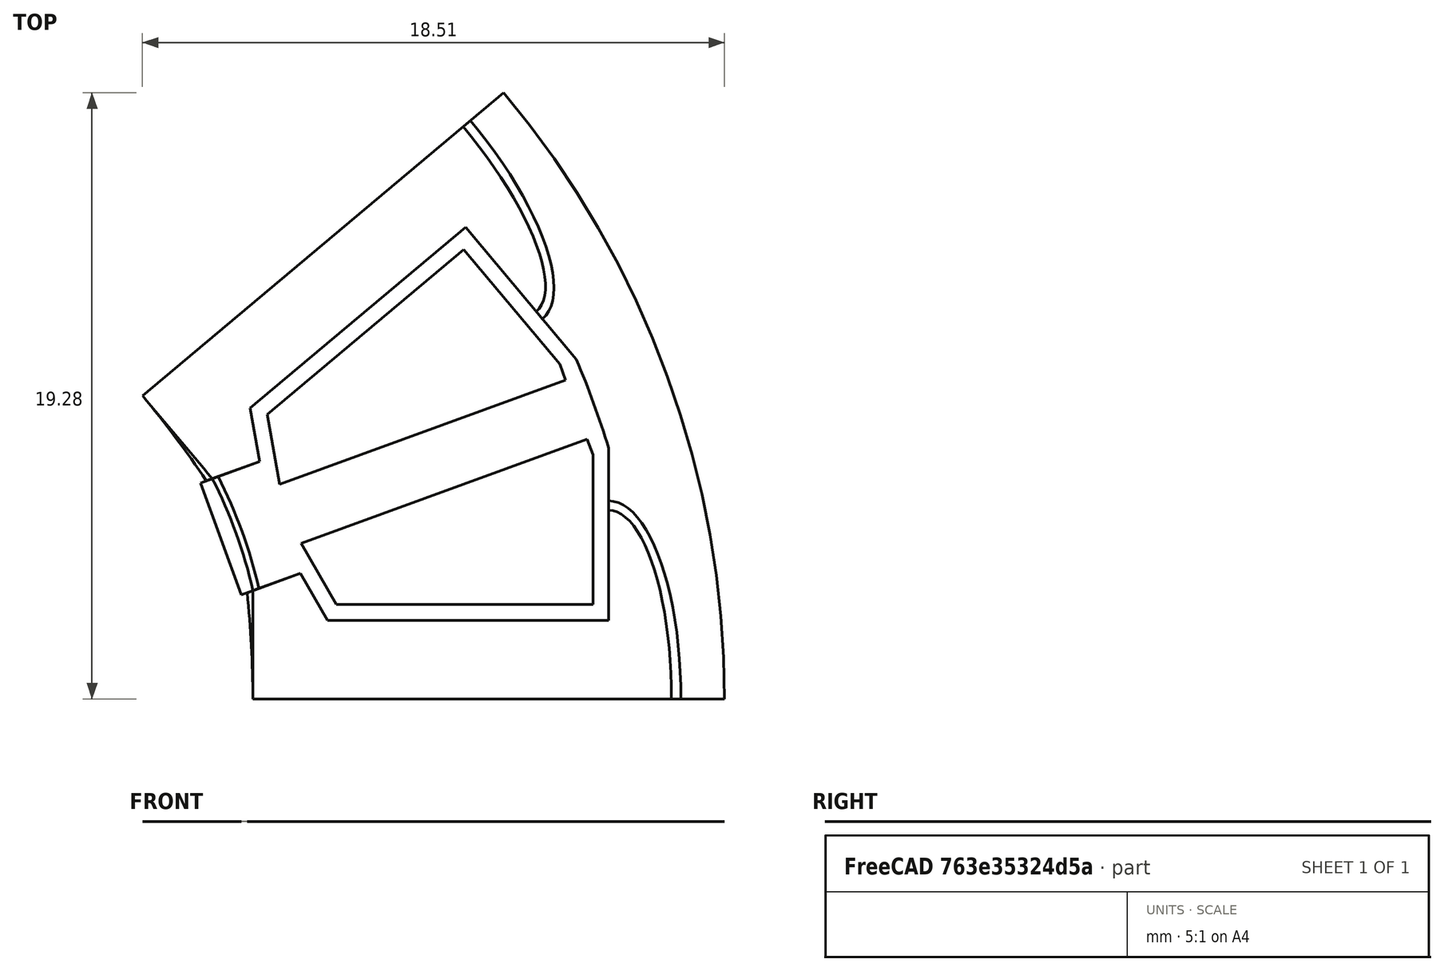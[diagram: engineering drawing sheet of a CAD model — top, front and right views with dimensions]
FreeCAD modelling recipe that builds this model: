
FCSTD DOCUMENT  (FreeCAD 0.18R4 (GitTag))
Label: StatorIRSpokeEllipse
License: All rights reserved
LicenseURL: http://en.wikipedia.org/wiki/All_rights_reserved
objects: Sketcher::SketchObject×10, Surface::Filling×8, PartDesign::Body×2, Spreadsheet::Sheet×1
note: 20 computed .brp shape members not serialized (recipe doc carries the construction recipe); baked Part::Feature solids carry a one-line shape summary decoded from their .brp

FEATURE [Spreadsheet::Sheet] Spreadsheet  label="Variables"
  cells = A2=slotNumber; B2(slotNumber)=9; A3=outerDiameter; B3(outerDiameter)=60; A4=innerDiameter; B4(innerDiameter)=30; A5=stackLength; B5(stackLength)=20; A6=stackingFactor; B6(stackingFactor)=0.95; A7=cuttingThickness; B7(cuttingThickness)=0.1; A8=skewAngle; B8(skewAngle)=0; A9=segmentAngle; B9(segmentAngle)==360 / slotNumber; A10=tipHeightReduction; B10(tipHeightReduction)=20; C10=%; A11=toothThickness; B11(toothThickness)=5; A12=yokeThickness; B12(yokeThickness)=2.5; A13=tipHeight; B13(tipHeight)=2; A14=tipAngle; B14(tipAngle)=120; A15=openingLeft; B15(openingLeft)=1.9; A16=openingRight; B16(openingRight)=1.9; A17=slotIsolation; B17(slotIsolation)=0.5; A18=windingAngle; B18(windingAngle)=35; A19=heightRatio; B19(heightRatio)=45; A20=roundingRadii; B20(roundingRadii)=0.2; A21=backWidth; B21(backWidth)=3; A22=backAngle; B22(backAngle)=90; A23=phaseSeparation; B23(phaseSeparation)=2; A24=axialOverhang; B24(axialOverhang)=1.2; A25=axialHeight; B25(axialHeight)=3; A26=spokeBridgeHeight; B26(spokeBridgeHeight)=0.2; A27=connectionHeight; B27(connectionHeight)=2; A28=connectionWidth; B28(connectionWidth)=12; A29=connectionThickness; B29(connectionThickness)=0.3
FEATURE [Sketcher::SketchObject] Sketch003  label="StatorSketch1"
  MapMode = 5
  Support = -> [XY_Plane]
  expr: Constraints[76] = Variables.backWidth
  expr: Constraints[37] = Variables.tipAngle
  expr: Constraints[60] = Variables.backAngle
  expr: Constraints[30] = Variables.tipHeight
  expr: Constraints[28] = Variables.openingRight
  expr: Constraints[32] = Variables.tipHeight * (1 - Variables.tipHeightReduction / 100)
  expr: Constraints[22] = Variables.openingLeft
  expr: Constraints[6] = Variables.outerDiameter / 2
  expr: Constraints[59] = Variables.tipHeight
  expr: Constraints[5] = Variables.segmentAngle
  expr: Constraints[11] = Variables.innerDiameter / 2
  expr: Constraints[54] = Variables.outerDiameter / 2 - Variables.yokeThickness
  expr: Constraints[49] = Variables.tipHeight * (1 - Variables.tipHeightReduction / 100)
  expr: Constraints[58] = Variables.toothThickness / 2
  expr: Constraints[18] = Variables.segmentAngle / 2
  expr: Constraints[50] = Variables.tipAngle
  expr: Constraints[52] = Variables.backAngle
  expr: Constraints[42] = Variables.toothThickness / 2
  sketch-geometry (27):
    g0: LineSegment [constr] StartX=0 StartY=0 StartZ=0 EndX=22.9813 EndY=19.2836 EndZ=0
    g1: LineSegment [constr] StartX=0 StartY=0 StartZ=0 EndX=30 EndY=0 EndZ=0
    g2: ArcOfCircle CenterX=0 CenterY=0 CenterZ=0 NormalX=0 NormalY=0 NormalZ=1 AngleXU=0 Radius=30 StartAngle=0 EndAngle=0.698132
    g3: ArcOfCircle [constr] CenterX=0 CenterY=0 CenterZ=0 NormalX=0 NormalY=0 NormalZ=1 AngleXU=0 Radius=15 StartAngle=0 EndAngle=0.698132
    g4: LineSegment [constr] StartX=13.3338 StartY=6.87098 StartZ=0 EndX=27.4859 EndY=12.0219 EndZ=0
    g5: LineSegment [constr] StartX=14.6308 StartY=3.30731 StartZ=0 EndX=28.7829 EndY=8.45826 EndZ=0
    g6: LineSegment [constr] StartX=28.1908 StartY=10.2606 StartZ=0 EndX=14.0954 EndY=5.1303 EndZ=0
    g7: LineSegment [constr] StartX=0 StartY=0 StartZ=0 EndX=14.0954 EndY=5.1303 EndZ=0
    g8: LineSegment [constr] StartX=13.3338 StartY=6.87098 StartZ=0 EndX=14.0954 EndY=5.1303 EndZ=0
    g9: LineSegment [constr] StartX=14.0954 StartY=5.1303 StartZ=0 EndX=14.6308 EndY=3.30731 EndZ=0
    g10: LineSegment [constr] StartX=13.5217 StartY=6.93938 StartZ=0 EndX=15.2132 EndY=7.55502 EndZ=0
    g11: LineSegment StartX=13.5217 StartY=6.93938 StartZ=0 EndX=15.2132 EndY=7.55502 EndZ=0
    g12: LineSegment StartX=15.2132 StartY=7.55502 StartZ=0 EndX=14.9141 EndY=9.25092 EndZ=0
    g13: LineSegment StartX=14.9141 StartY=9.25092 StartZ=0 EndX=21.7663 EndY=15.0006 EndZ=0
    g14: LineSegment [constr] StartX=14.9141 StartY=9.25092 StartZ=0 EndX=13.3072 EndY=11.166 EndZ=0
    g15: LineSegment StartX=21.7663 StartY=15.0006 StartZ=0 EndX=25.29 EndY=10.8011 EndZ=0
    g16: LineSegment StartX=26.3161 StartY=7.98201 StartZ=0 EndX=26.3161 EndY=2.5 EndZ=0
    g17: LineSegment StartX=26.3161 StartY=2.5 StartZ=0 EndX=17.3713 EndY=2.5 EndZ=0
    g18: LineSegment StartX=17.3713 StartY=2.5 StartZ=0 EndX=16.5102 EndY=3.99135 EndZ=0
    g19: LineSegment StartX=16.5102 StartY=3.99135 StartZ=0 EndX=14.8188 EndY=3.37572 EndZ=0
    g20: LineSegment [constr] StartX=26.3161 StartY=2.5 StartZ=0 EndX=26.3161 EndY=0 EndZ=0
    g21: LineSegment StartX=11.4907 StartY=9.64181 StartZ=0 EndX=22.9813 EndY=19.2836 EndZ=0
    g22: LineSegment StartX=30 StartY=0 StartZ=0 EndX=15 EndY=0 EndZ=0
    g23: ArcOfCircle CenterX=-16.5325 CenterY=0 CenterZ=0 NormalX=0 NormalY=0 NormalZ=1 AngleXU=0 Radius=31.5325 StartAngle=0 EndAngle=0.107261
    g24: ArcOfCircle CenterX=-12.6646 CenterY=-10.6269 CenterZ=0 NormalX=0 NormalY=0 NormalZ=1 AngleXU=0 Radius=31.5325 StartAngle=0.590871 EndAngle=0.698132
    g25: ArcOfCircle CenterX=0 CenterY=0 CenterZ=0 NormalX=0 NormalY=0 NormalZ=1 AngleXU=0 Radius=27.5 StartAngle=0.294493 EndAngle=0.403638
    g26: LineSegment [constr] StartX=25.29 StartY=10.8011 StartZ=0 EndX=26.3161 EndY=7.98201 EndZ=0
  constraints (77):
    c: Angle(g-1,g1) = 0
    c: Coincident(g0,g-1)
    c: Coincident(g1,g-1)
    c: Coincident(g2,g-1)
    c: Coincident(g2,g0)
    c: Angle(g1,g0) = 0.698132
    c: Radius(g2) = 30
    c: Coincident(g2,g1)
    c: Coincident(g3,g-1)
    c: PointOnObject(g3,g1)
    c: PointOnObject(g3,g0)
    c: Radius(g3) = 15
    c: PointOnObject(g4,g3)
    c: PointOnObject(g4,g2)
    c: PointOnObject(g5,g3)
    c: PointOnObject(g5,g2)
    c: PointOnObject(g6,g2)
    c: PointOnObject(g6,g3)
    c: Angle(g1,g6) = 0.349066
    c: Coincident(g7,g-1)
    c: Coincident(g7,g6)
    c: Coincident(g8,g4)
    c: Distance(g8) = 1.9
    c: Coincident(g8,g6)
    c: Parallel(g4,g6)
    c: Parallel(g5,g6)
    c: Coincident(g9,g6)
    c: Coincident(g9,g5)
    c: Distance(g9) = 1.9
    c: PointOnObject(g10,g4)
    c: Distance(g4,g10) = 2
    c: Angle(g4,g10) = 3.14159
    c: Distance(g10,g10) = 1.6
    c: Coincident(g11,g10)
    c: Coincident(g12,g11)
    c: Coincident(g13,g12)
    c: Coincident(g11,g10)
    c: Angle(g12,g13) = 2.0944
    c: Parallel(g0,g13)
    c: Coincident(g14,g12)
    c: PointOnObject(g14,g0)
    c: Angle(g13,g14) = 1.5708
    c: Distance(g14) = 2.5
    c: Coincident(g15,g13)
    c: Coincident(g17,g16)
    c: Coincident(g18,g17)
    c: PointOnObject(g18,g5)
    c: Coincident(g19,g18)
    c: PointOnObject(g19,g5)
    c: Distance(g19) = 1.6
    c: Angle(g17,g18) = 2.0944
    c: Parallel(g17,g1)
    c: Angle(g16,g17) = 1.5708
    c: Symmetric(g15,g16,g6)
    c: Distance(g-1,g15) = 27.5
    c: Coincident(g20,g16)
    c: PointOnObject(g20,g1)
    c: Vertical(g20)
    c: DistanceY(g20,g20) = 2.5
    c: Distance(g5,g18) = 2
    c: Angle(g13,g15) = 1.5708
    c: Coincident(g21,g3)
    c: Coincident(g21,g0)
    c: Coincident(g22,g2)
    c: Coincident(g22,g3)
    c: PointOnObject(g23,g-1)
    c: Coincident(g23,g19)
    c: Coincident(g23,g22)
    c: PointOnObject(g24,g0)
    c: Coincident(g24,g11)
    c: Coincident(g24,g21)
    c: Coincident(g25,g2)
    c: Coincident(g25,g15)
    c: Coincident(g25,g16)
    c: Coincident(g26,g15)
    c: Coincident(g26,g16)
    c: Distance(g26) = 3
FEATURE [Sketcher::SketchObject] Sketch  label="StatorStack"
  MapMode = 5
  Support = -> [XY_Plane001]
  expr: Constraints[20] = Variables.innerDiameter / 2
  expr: Constraints[10] = Variables.outerDiameter / 2
  expr: Constraints[9] = Variables.innerDiameter / 2
  expr: Constraints[8] = Variables.stackLength
  sketch-geometry (8):
    g0: LineSegment StartX=-10 StartY=15 StartZ=0 EndX=10 EndY=15 EndZ=0
    g1: LineSegment StartX=10 StartY=15 StartZ=0 EndX=10 EndY=30 EndZ=0
    g2: LineSegment StartX=10 StartY=30 StartZ=0 EndX=-10 EndY=30 EndZ=0
    g3: LineSegment StartX=-10 StartY=30 StartZ=0 EndX=-10 EndY=15 EndZ=0
    g4: LineSegment StartX=-10 StartY=-15 StartZ=0 EndX=10 EndY=-15 EndZ=0
    g5: LineSegment StartX=10 StartY=-15 StartZ=0 EndX=10 EndY=-30 EndZ=0
    g6: LineSegment StartX=10 StartY=-30 StartZ=0 EndX=-10 EndY=-30 EndZ=0
    g7: LineSegment StartX=-10 StartY=-30 StartZ=0 EndX=-10 EndY=-15 EndZ=0
  constraints (22):
    c: Coincident(g0,g1)
    c: Coincident(g1,g2)
    c: Coincident(g2,g3)
    c: Coincident(g3,g0)
    c: Horizontal(g2)
    c: Vertical(g1)
    c: Vertical(g3)
    c: Symmetric(g0,g0,g-2)
    c: DistanceX(g0,g0) = 20
    c: DistanceY(g-1,g0) = 15
    c: DistanceY(g-1,g1) = 30
    c: Coincident(g4,g5)
    c: Coincident(g5,g6)
    c: Coincident(g6,g7)
    c: Coincident(g7,g4)
    c: Horizontal(g6)
    c: Vertical(g5)
    c: Vertical(g7)
    c: Equal(g4,g0)
    c: Symmetric(g4,g4,g-2)
    c: DistanceY(g4,g-1) = 15
    c: Equal(g7,g3)
FEATURE [Sketcher::SketchObject] Sketch005  label="StatorSketch2"
  MapMode = 5
  Support = -> [XY_Plane]
  expr: Constraints[76] = Variables.backWidth
  expr: Constraints[30] = Variables.tipHeight
  expr: Constraints[51] = Variables.tipAngle
  expr: Constraints[28] = Variables.openingRight
  expr: Constraints[37] = Variables.tipAngle
  expr: Constraints[60] = Variables.tipHeight
  expr: Constraints[32] = Variables.tipHeight * (1 - Variables.tipHeightReduction / 100)
  expr: Constraints[61] = Variables.backAngle
  expr: Constraints[6] = Variables.outerDiameter / 2
  expr: Constraints[5] = Variables.segmentAngle
  expr: Constraints[22] = Variables.openingLeft
  expr: Constraints[55] = Variables.outerDiameter / 2 - Variables.yokeThickness
  expr: Constraints[59] = Variables.toothThickness / 2
  expr: Constraints[50] = Variables.tipHeight * (1 - Variables.tipHeightReduction / 100)
  expr: Constraints[18] = Variables.segmentAngle / 2
  expr: Constraints[11] = Variables.innerDiameter / 2
  expr: Constraints[53] = Variables.backAngle
  expr: Constraints[42] = Variables.toothThickness / 2
  sketch-geometry (27):
    g0: LineSegment [constr] StartX=0 StartY=0 StartZ=0 EndX=22.9813 EndY=19.2836 EndZ=0
    g1: LineSegment [constr] StartX=0 StartY=0 StartZ=0 EndX=30 EndY=0 EndZ=0
    g2: ArcOfCircle CenterX=0 CenterY=0 CenterZ=0 NormalX=0 NormalY=0 NormalZ=1 AngleXU=0 Radius=30 StartAngle=0 EndAngle=0.698132
    g3: ArcOfCircle [constr] CenterX=0 CenterY=0 CenterZ=0 NormalX=0 NormalY=0 NormalZ=1 AngleXU=0 Radius=15 StartAngle=0 EndAngle=0.698132
    g4: LineSegment [constr] StartX=13.3338 StartY=6.87098 StartZ=0 EndX=27.4859 EndY=12.0219 EndZ=0
    g5: LineSegment [constr] StartX=14.6308 StartY=3.30731 StartZ=0 EndX=28.7829 EndY=8.45826 EndZ=0
    g6: LineSegment [constr] StartX=28.1908 StartY=10.2606 StartZ=0 EndX=14.0954 EndY=5.1303 EndZ=0
    g7: LineSegment [constr] StartX=0 StartY=0 StartZ=0 EndX=14.0954 EndY=5.1303 EndZ=0
    g8: LineSegment [constr] StartX=13.3338 StartY=6.87098 StartZ=0 EndX=14.0954 EndY=5.1303 EndZ=0
    g9: LineSegment [constr] StartX=14.0954 StartY=5.1303 StartZ=0 EndX=14.6308 EndY=3.30731 EndZ=0
    g10: LineSegment [constr] StartX=13.7097 StartY=7.00779 StartZ=0 EndX=15.2132 EndY=7.55502 EndZ=0
    g11: LineSegment StartX=13.7097 StartY=7.00779 StartZ=0 EndX=15.2132 EndY=7.55502 EndZ=0
    g12: LineSegment StartX=15.2132 StartY=7.55502 StartZ=0 EndX=14.9141 EndY=9.25092 EndZ=0
    g13: LineSegment StartX=14.9141 StartY=9.25092 StartZ=0 EndX=21.7663 EndY=15.0006 EndZ=0
    g14: LineSegment [constr] StartX=14.9141 StartY=9.25092 StartZ=0 EndX=13.3072 EndY=11.166 EndZ=0
    g15: LineSegment StartX=21.7663 StartY=15.0006 StartZ=0 EndX=25.29 EndY=10.8011 EndZ=0
    g16: LineSegment [constr] StartX=25.29 StartY=10.8011 StartZ=0 EndX=26.3161 EndY=7.98201 EndZ=0
    g17: LineSegment StartX=26.3161 StartY=7.98201 StartZ=0 EndX=26.3161 EndY=2.5 EndZ=0
    g18: LineSegment StartX=26.3161 StartY=2.5 StartZ=0 EndX=17.3713 EndY=2.5 EndZ=0
    g19: LineSegment StartX=17.3713 StartY=2.5 StartZ=0 EndX=16.5102 EndY=3.99135 EndZ=0
    g20: LineSegment StartX=16.5102 StartY=3.99135 StartZ=0 EndX=15.0067 EndY=3.44412 EndZ=0
    g21: LineSegment [constr] StartX=26.3161 StartY=2.5 StartZ=0 EndX=26.3161 EndY=0 EndZ=0
    g22: LineSegment StartX=11.4907 StartY=9.64181 StartZ=0 EndX=22.9813 EndY=19.2836 EndZ=0
    g23: LineSegment StartX=30 StartY=0 StartZ=0 EndX=15 EndY=1.08e-13 EndZ=0
    g24: ArcOfCircle CenterX=687.223 CenterY=576.649 CenterZ=0 NormalX=0 NormalY=0 NormalZ=1 AngleXU=0 Radius=882.106 StartAngle=3.83972 EndAngle=3.84363
    g25: ArcOfCircle CenterX=897.106 CenterY=0 CenterZ=0 NormalX=0 NormalY=0 NormalZ=1 AngleXU=0 Radius=882.106 StartAngle=3.13769 EndAngle=3.14159
    g26: ArcOfCircle CenterX=0 CenterY=0 CenterZ=0 NormalX=0 NormalY=0 NormalZ=1 AngleXU=0 Radius=27.5 StartAngle=0.294493 EndAngle=0.403638
  constraints (77):
    c: Angle(g-1,g1) = 0
    c: Coincident(g0,g-1)
    c: Coincident(g1,g-1)
    c: Coincident(g2,g-1)
    c: Coincident(g2,g0)
    c: Angle(g1,g0) = 0.698132
    c: Radius(g2) = 30
    c: Coincident(g2,g1)
    c: Coincident(g3,g-1)
    c: PointOnObject(g3,g1)
    c: PointOnObject(g3,g0)
    c: Radius(g3) = 15
    c: PointOnObject(g4,g3)
    c: PointOnObject(g4,g2)
    c: PointOnObject(g5,g3)
    c: PointOnObject(g5,g2)
    c: PointOnObject(g6,g2)
    c: PointOnObject(g6,g3)
    c: Angle(g1,g6) = 0.349066
    c: Coincident(g7,g-1)
    c: Coincident(g7,g6)
    c: Coincident(g8,g4)
    c: Distance(g8) = 1.9
    c: Coincident(g8,g6)
    c: Parallel(g4,g6)
    c: Parallel(g5,g6)
    c: Coincident(g9,g6)
    c: Coincident(g9,g5)
    c: Distance(g9) = 1.9
    c: PointOnObject(g10,g4)
    c: Distance(g4,g10) = 2
    c: Angle(g4,g10) = 3.14159
    c: Distance(g10,g10) = 1.6
    c: Coincident(g11,g10)
    c: Coincident(g12,g11)
    c: Coincident(g13,g12)
    c: Coincident(g11,g10)
    c: Angle(g12,g13) = 2.0944
    c: Parallel(g0,g13)
    c: Coincident(g14,g12)
    c: PointOnObject(g14,g0)
    c: Angle(g13,g14) = 1.5708
    c: Distance(g14) = 2.5
    c: Coincident(g15,g13)
    c: Coincident(g16,g15)
    c: Coincident(g17,g16)
    c: Coincident(g18,g17)
    c: Coincident(g19,g18)
    c: PointOnObject(g19,g5)
    c: Coincident(g20,g19)
    c: Distance(g20) = 1.6
    c: Angle(g18,g19) = 2.0944
    c: Parallel(g18,g1)
    c: Angle(g17,g18) = 1.5708
    c: Symmetric(g15,g16,g6)
    c: Distance(g-1,g15) = 27.5
    c: Coincident(g21,g17)
    c: PointOnObject(g21,g1)
    c: Vertical(g21)
    c: DistanceY(g21,g21) = 2.5
    c: Distance(g5,g19) = 2
    c: Angle(g13,g15) = 1.5708
    c: Coincident(g22,g3)
    c: Coincident(g22,g0)
    c: Coincident(g23,g2)
    c: Coincident(g23,g3)
    c: PointOnObject(g24,g22)
    c: Coincident(g24,g11)
    c: Coincident(g24,g22)
    c: Angle(g5,g20) = 3.14159
    c: PointOnObject(g25,g-1)
    c: Coincident(g25,g20)
    c: Coincident(g25,g23)
    c: Coincident(g26,g2)
    c: Coincident(g26,g15)
    c: Coincident(g26,g17)
    c: Distance(g16) = 3
FEATURE [Sketcher::SketchObject] Sketch008  label="SlotSketch"
  MapMode = 5
  Support = -> [XY_Plane]
  expr: Constraints[50] = Variables.toothThickness / 2
  expr: Constraints[18] = Variables.segmentAngle / 2
  expr: Constraints[30] = Variables.tipAngle
  expr: Constraints[51] = Variables.tipHeight
  expr: Constraints[28] = Variables.openingRight
  expr: Constraints[67] = Variables.backWidth
  expr: Constraints[46] = Variables.outerDiameter / 2 - Variables.yokeThickness
  expr: Constraints[22] = Variables.openingLeft
  expr: Constraints[6] = Variables.outerDiameter / 2
  expr: Constraints[44] = Variables.backAngle
  expr: Constraints[52] = Variables.backAngle
  expr: Constraints[11] = Variables.innerDiameter / 2
  expr: Constraints[5] = Variables.segmentAngle
  expr: Constraints[42] = Variables.tipAngle
  expr: Constraints[35] = Variables.toothThickness / 2
  sketch-geometry (25):
    g0: LineSegment [constr] StartX=0 StartY=0 StartZ=0 EndX=22.9813 EndY=19.2836 EndZ=0
    g1: LineSegment [constr] StartX=0 StartY=0 StartZ=0 EndX=30 EndY=0 EndZ=0
    g2: ArcOfCircle [constr] CenterX=0 CenterY=0 CenterZ=0 NormalX=0 NormalY=0 NormalZ=1 AngleXU=0 Radius=30 StartAngle=0 EndAngle=0.698132
    g3: ArcOfCircle [constr] CenterX=0 CenterY=0 CenterZ=0 NormalX=0 NormalY=0 NormalZ=1 AngleXU=0 Radius=15 StartAngle=0 EndAngle=0.698132
    g4: LineSegment [constr] StartX=13.3338 StartY=6.87098 StartZ=0 EndX=27.4859 EndY=12.0219 EndZ=0
    g5: LineSegment [constr] StartX=14.6308 StartY=3.30731 StartZ=0 EndX=28.7829 EndY=8.45826 EndZ=0
    g6: LineSegment [constr] StartX=28.1908 StartY=10.2606 StartZ=0 EndX=14.0954 EndY=5.1303 EndZ=0
    g7: LineSegment [constr] StartX=0 StartY=0 StartZ=0 EndX=14.0954 EndY=5.1303 EndZ=0
    g8: LineSegment [constr] StartX=13.3338 StartY=6.87098 StartZ=0 EndX=14.0954 EndY=5.1303 EndZ=0
    g9: LineSegment [constr] StartX=14.0954 StartY=5.1303 StartZ=0 EndX=14.6308 EndY=3.30731 EndZ=0
    g10: LineSegment StartX=15.2132 StartY=7.55502 StartZ=0 EndX=14.9141 EndY=9.25092 EndZ=0
    g11: LineSegment StartX=14.9141 StartY=9.25092 StartZ=0 EndX=21.7663 EndY=15.0006 EndZ=0
    g12: LineSegment [constr] StartX=14.9141 StartY=9.25092 StartZ=0 EndX=13.3072 EndY=11.166 EndZ=0
    g13: LineSegment StartX=21.7663 StartY=15.0006 StartZ=0 EndX=25.29 EndY=10.8011 EndZ=0
    g14: LineSegment [constr] StartX=25.29 StartY=10.8011 StartZ=0 EndX=26.3161 EndY=7.98201 EndZ=0
    g15: LineSegment StartX=26.3161 StartY=7.98201 StartZ=0 EndX=26.3161 EndY=2.5 EndZ=0
    g16: LineSegment StartX=26.3161 StartY=2.5 StartZ=0 EndX=17.3713 EndY=2.5 EndZ=0
    g17: LineSegment StartX=17.3713 StartY=2.5 StartZ=0 EndX=16.5102 EndY=3.99135 EndZ=0
    g18: LineSegment [constr] StartX=26.3161 StartY=2.5 StartZ=0 EndX=26.3161 EndY=0 EndZ=0
    g19: LineSegment [constr] StartX=11.4907 StartY=9.64181 StartZ=0 EndX=22.9813 EndY=19.2836 EndZ=0
    g20: LineSegment [constr] StartX=30 StartY=0 StartZ=0 EndX=15 EndY=0 EndZ=0
    g21: LineSegment StartX=13.3338 StartY=6.87098 StartZ=0 EndX=14.6308 EndY=3.30731 EndZ=0
    g22: LineSegment StartX=13.3338 StartY=6.87098 StartZ=0 EndX=15.2132 EndY=7.55502 EndZ=0
    g23: LineSegment StartX=14.6308 StartY=3.30731 StartZ=0 EndX=16.5102 EndY=3.99135 EndZ=0
    g24: ArcOfCircle CenterX=0 CenterY=0 CenterZ=0 NormalX=0 NormalY=0 NormalZ=1 AngleXU=0 Radius=27.5 StartAngle=0.294493 EndAngle=0.403638
  constraints (68):
    c: Angle(g-1,g1) = 0
    c: Coincident(g0,g-1)
    c: Coincident(g1,g-1)
    c: Coincident(g2,g-1)
    c: Coincident(g2,g0)
    c: Angle(g1,g0) = 0.698132
    c: Radius(g2) = 30
    c: Coincident(g2,g1)
    c: Coincident(g3,g-1)
    c: PointOnObject(g3,g1)
    c: PointOnObject(g3,g0)
    c: Radius(g3) = 15
    c: PointOnObject(g4,g3)
    c: PointOnObject(g4,g2)
    c: PointOnObject(g5,g3)
    c: PointOnObject(g5,g2)
    c: PointOnObject(g6,g2)
    c: PointOnObject(g6,g3)
    c: Angle(g1,g6) = 0.349066
    c: Coincident(g7,g-1)
    c: Coincident(g7,g6)
    c: Coincident(g8,g4)
    c: Distance(g8) = 1.9
    c: Coincident(g8,g6)
    c: Parallel(g4,g6)
    c: Parallel(g5,g6)
    c: Coincident(g9,g6)
    c: Coincident(g9,g5)
    c: Distance(g9) = 1.9
    c: Coincident(g11,g10)
    c: Angle(g10,g11) = 2.0944
    c: Parallel(g0,g11)
    c: Coincident(g12,g10)
    c: PointOnObject(g12,g0)
    c: Angle(g11,g12) = 1.5708
    c: Distance(g12) = 2.5
    c: Coincident(g13,g11)
    c: Coincident(g14,g13)
    c: Coincident(g15,g14)
    c: Coincident(g16,g15)
    c: Coincident(g17,g16)
    c: PointOnObject(g17,g5)
    c: Angle(g16,g17) = 2.0944
    c: Parallel(g16,g1)
    c: Angle(g15,g16) = 1.5708
    c: Symmetric(g13,g14,g6)
    c: Distance(g-1,g13) = 27.5
    c: Coincident(g18,g15)
    c: PointOnObject(g18,g1)
    c: Vertical(g18)
    c: DistanceY(g18,g18) = 2.5
    c: Distance(g5,g17) = 2
    c: Angle(g11,g13) = 1.5708
    c: Coincident(g19,g3)
    c: Coincident(g19,g0)
    c: Coincident(g20,g2)
    c: Coincident(g20,g3)
    c: Symmetric(g17,g10,g6)
    c: Coincident(g21,g4)
    c: Coincident(g21,g5)
    c: Coincident(g22,g21)
    c: Coincident(g22,g10)
    c: Coincident(g23,g21)
    c: Coincident(g23,g17)
    c: Coincident(g24,g-1)
    c: Coincident(g24,g13)
    c: Coincident(g24,g15)
    c: Distance(g14) = 3
FEATURE [Sketcher::SketchObject] Sketch006  label="TerminalLeftSketch"
  ExternalGeometry = -> [Sketch008]
  MapMode = 5
  Support = -> [XY_Plane]
  expr: Constraints[28] = abs(Variables.backWidth - Variables.phaseSeparation) / 2 + Variables.slotIsolation / 15
  expr: Constraints[21] = Variables.slotIsolation
  expr: Constraints[14] = Variables.phaseSeparation / 2
  sketch-geometry (10):
    g0: LineSegment StartX=24.7672 StartY=10.6463 StartZ=0 EndX=21.7046 EndY=14.2961 EndZ=0
    g1: LineSegment StartX=21.7046 StartY=14.2961 StartZ=0 EndX=15.4567 EndY=9.05346 EndZ=0
    g2: LineSegment StartX=15.4567 StartY=9.05346 StartZ=0 EndX=15.8483 EndY=6.83248 EndZ=0
    g3: LineSegment StartX=15.8483 StartY=6.83248 StartZ=0 EndX=24.9497 EndY=10.1451 EndZ=0
    g4: LineSegment StartX=24.9497 StartY=10.1451 StartZ=0 EndX=24.7672 EndY=10.6463 EndZ=0
    g5: LineSegment [constr] StartX=0 StartY=0 StartZ=0 EndX=15.8617 EndY=5.77319 EndZ=0
    g6: LineSegment [constr] StartX=15.8483 StartY=6.83248 StartZ=0 EndX=16.1903 EndY=5.89279 EndZ=0
    g7: LineSegment [constr] StartX=21.7046 StartY=14.2961 StartZ=0 EndX=22.0877 EndY=14.6175 EndZ=0
    g8: LineSegment [constr] StartX=21.7046 StartY=14.2961 StartZ=0 EndX=21.3833 EndY=14.6792 EndZ=0
    g9: LineSegment [constr] StartX=15.4567 StartY=9.05346 StartZ=0 EndX=14.9643 EndY=8.96663 EndZ=0
  constraints (29):
    c: Coincident(g1,g0)
    c: Coincident(g2,g1)
    c: Coincident(g3,g2)
    c: Coincident(g4,g3)
    c: Coincident(g4,g0)
    c: Parallel(g1,g-4)
    c: Parallel(g-5,g2)
    c: Parallel(g0,g-3)
    c: Angle(g4,g3) = 1.5708
    c: Symmetric(g-5,g-6,g5)
    c: Parallel(g3,g5)
    c: Coincident(g6,g2)
    c: PointOnObject(g6,g5)
    c: Angle(g6,g5) = 1.5708
    c: Distance(g6) = 1
    c: Coincident(g7,g0)
    c: PointOnObject(g7,g-3)
    c: Coincident(g8,g0)
    c: PointOnObject(g8,g-4)
    c: Angle(g0,g7) = 1.5708
    c: Angle(g8,g1) = 1.5708
    c: Distance(g8) = 0.5
    c: Equal(g8,g7)
    c: Coincident(g5,g-1)
    c: Coincident(g9,g1)
    c: PointOnObject(g9,g-5)
    c: Angle(g-5,g9) = 1.5708
    c: Equal(g8,g9)
    c: Distance(g4) = 0.533333
FEATURE [Sketcher::SketchObject] Sketch007  label="TerminalRightSketch"
  ExternalGeometry = -> [Sketch008]
  MapMode = 5
  Support = -> [XY_Plane]
  expr: Constraints[27] = Variables.slotIsolation
  expr: Constraints[26] = abs(Variables.backWidth - Variables.phaseSeparation) / 2 + Variables.slotIsolation / 15
  expr: Constraints[13] = Variables.phaseSeparation / 2
  sketch-geometry (10):
    g0: LineSegment [constr] StartX=0 StartY=0 StartZ=0 EndX=15.8617 EndY=5.77319 EndZ=0
    g1: LineSegment StartX=25.8161 StartY=7.76456 StartZ=0 EndX=25.8161 EndY=3 EndZ=0
    g2: LineSegment StartX=25.8161 StartY=3 StartZ=0 EndX=17.6599 EndY=3 EndZ=0
    g3: LineSegment StartX=17.6599 StartY=3 StartZ=0 EndX=16.5323 EndY=4.95309 EndZ=0
    g4: LineSegment StartX=16.5323 StartY=4.95309 StartZ=0 EndX=25.6337 EndY=8.26572 EndZ=0
    g5: LineSegment StartX=25.6337 StartY=8.26572 StartZ=0 EndX=25.8161 EndY=7.76456 EndZ=0
    g6: LineSegment [constr] StartX=16.5323 StartY=4.95309 StartZ=0 EndX=16.1903 EndY=5.89279 EndZ=0
    g7: LineSegment [constr] StartX=25.8161 StartY=3 StartZ=0 EndX=25.8161 EndY=2.5 EndZ=0
    g8: LineSegment [constr] StartX=25.8161 StartY=3 StartZ=0 EndX=26.3161 EndY=3 EndZ=0
    g9: LineSegment [constr] StartX=17.6599 StartY=3 StartZ=0 EndX=17.2269 EndY=2.75 EndZ=0
  constraints (29):
    c: Symmetric(g-5,g-6,g0)
    c: Coincident(g0,g-1)
    c: Vertical(g1)
    c: Coincident(g2,g1)
    c: Horizontal(g2)
    c: Coincident(g3,g2)
    c: Coincident(g4,g3)
    c: Coincident(g5,g4)
    c: Coincident(g5,g1)
    c: Parallel(g0,g4)
    c: Coincident(g6,g3)
    c: PointOnObject(g6,g0)
    c: Angle(g0,g6) = 1.5708
    c: Distance(g6) = 1
    c: Angle(g4,g5) = 1.5708
    c: Coincident(g7,g1)
    c: PointOnObject(g7,g-7)
    c: Coincident(g8,g1)
    c: PointOnObject(g8,g-8)
    c: Angle(g8,g1) = 1.5708
    c: Angle(g2,g7) = 1.5708
    c: Equal(g8,g7)
    c: Parallel(g3,g-6)
    c: Coincident(g9,g2)
    c: PointOnObject(g9,g-6)
    c: Angle(g3,g9) = 1.5708
    c: Distance(g5) = 0.533333
    c: Distance(g8) = 0.5
    c: Equal(g8,g9)
FEATURE [Surface::Filling] Surface  label="SlotSketch_Surface"
  Anisotropy = false
  BoundaryEdges = -> [Sketch008]
  BoundaryOrder = [0,0,0,0,0,0,0,0,0,0]
  Degree = 3
  Iterations = 2
  MaximumDegree = 8
  MaximumSegments = 9
  PointsOnCurve = 15
  TolAngular = 0.01
  TolCurvature = 0.1
  Tolerance2d = 1e-05
  Tolerance3d = 0.0001
FEATURE [Surface::Filling] Surface001  label="StatorSketch2_Surface"
  Anisotropy = false
  BoundaryEdges = -> [Sketch005]
  BoundaryOrder = [0,0,0,0,0,0,0,0,0,0,0,0,0,0]
  Degree = 3
  Iterations = 2
  MaximumDegree = 8
  MaximumSegments = 9
  PointsOnCurve = 15
  TolAngular = 0.01
  TolCurvature = 0.1
  Tolerance2d = 1e-05
  Tolerance3d = 0.0001
FEATURE [Surface::Filling] Surface002  label="StatorSketch1_Surface"
  Anisotropy = false
  BoundaryEdges = -> [Sketch003]
  BoundaryOrder = [0,0,0,0,0,0,0,0,0,0,0,0,0,0]
  Degree = 3
  Iterations = 2
  MaximumDegree = 8
  MaximumSegments = 9
  PointsOnCurve = 15
  TolAngular = 0.01
  TolCurvature = 0.1
  Tolerance2d = 1e-05
  Tolerance3d = 0.0001
FEATURE [Surface::Filling] Surface003  label="TerminalRightSketch_Surface"
  Anisotropy = false
  BoundaryEdges = -> [Sketch007]
  BoundaryOrder = [0,0,0,0,0]
  Degree = 3
  Iterations = 2
  MaximumDegree = 8
  MaximumSegments = 9
  PointsOnCurve = 15
  TolAngular = 0.01
  TolCurvature = 0.1
  Tolerance2d = 1e-05
  Tolerance3d = 0.0001
FEATURE [Surface::Filling] Surface004  label="TerminalLeftSketch_Surface"
  Anisotropy = false
  BoundaryEdges = -> [Sketch006]
  BoundaryOrder = [0,0,0,0,0]
  Degree = 3
  Iterations = 2
  MaximumDegree = 8
  MaximumSegments = 9
  PointsOnCurve = 15
  TolAngular = 0.01
  TolCurvature = 0.1
  Tolerance2d = 1e-05
  Tolerance3d = 0.0001
FEATURE [Sketcher::SketchObject] Sketch010  label="ToothLine"
  ExternalGeometry = -> [Sketch008]
  MapMode = 5
  Support = -> [XY_Plane]
  expr: Constraints[0] = Variables.toothThickness
  sketch-geometry (1):
    g0: LineSegment StartX=18.3402 StartY=12.1257 StartZ=0 EndX=15.1263 EndY=15.956 EndZ=0
  constraints (3):
    c: Distance(g0) = 5
    c: Symmetric(g-3,g-3,g0)
    c: Angle(g-3,g0) = 1.5708
FEATURE [Sketcher::SketchObject] Sketch011  label="YokeLine"
  ExternalGeometry = -> [Sketch008]
  MapMode = 5
  Support = -> [XY_Plane]
  expr: Constraints[0] = Variables.yokeThickness
  sketch-geometry (3):
    g0: LineSegment [constr] StartX=25.29 StartY=10.8011 StartZ=0 EndX=26.3161 EndY=7.98201 EndZ=0
    g1: LineSegment StartX=25.8415 StartY=9.40555 StartZ=0 EndX=28.1908 EndY=10.2606 EndZ=0
    g2: LineSegment [constr] StartX=25.8415 StartY=9.40555 StartZ=0 EndX=25.8031 EndY=9.39155 EndZ=0
  constraints (8):
    c: Distance(g1) = 2.5
    c: Coincident(g2,g1)
    c: Angle(g0,g2) = 1.5708
    c: Symmetric(g0,g0,g2)
    c: Parallel(g2,g1)
    c: Coincident(g0,g-3)
    c: Coincident(g0,g-3)
    c: PointOnObject(g1,g-3)
FEATURE [Sketcher::SketchObject] Sketch012  label="Isolation"
  ExternalGeometry = -> [Sketch]
  MapMode = 5
  Support = -> [XY_Plane001]
  expr: Constraints[83] = Variables.axialHeight / 2
  expr: Constraints[19] = (Variables.outerDiameter - Variables.innerDiameter) / 2 - Variables.yokeThickness - Variables.tipHeight
  expr: Constraints[18] = Variables.yokeThickness
  expr: Constraints[17] = Variables.tipHeight
  expr: Constraints[16] = Variables.axialHeight
  expr: Constraints[15] = Variables.axialHeight + Variables.axialOverhang
  sketch-geometry (32):
    g0: LineSegment StartX=-10 StartY=30 StartZ=0 EndX=-10 EndY=15 EndZ=0
    g1: LineSegment StartX=-10 StartY=15 StartZ=0 EndX=-12.7 EndY=15 EndZ=0
    g2: LineSegment StartX=-12.7 StartY=15 StartZ=0 EndX=-12.7 EndY=17 EndZ=0
    g3: LineSegment StartX=-12.7 StartY=17 StartZ=0 EndX=-11.2 EndY=17 EndZ=0
    g4: LineSegment StartX=-11.2 StartY=17 StartZ=0 EndX=-11.2 EndY=27.5 EndZ=0
    g5: LineSegment StartX=-11.2 StartY=27.5 StartZ=0 EndX=-14.2 EndY=27.5 EndZ=0
    g6: LineSegment StartX=-14.2 StartY=27.5 StartZ=0 EndX=-14.2 EndY=30 EndZ=0
    g7: LineSegment StartX=-14.2 StartY=30 StartZ=0 EndX=-10 EndY=30 EndZ=0
    g8: LineSegment StartX=-12.7 StartY=-15 StartZ=0 EndX=-10 EndY=-15 EndZ=0
    g9: LineSegment StartX=-10 StartY=-15 StartZ=0 EndX=-10 EndY=-30 EndZ=0
    g10: LineSegment StartX=-10 StartY=-30 StartZ=0 EndX=-14.2 EndY=-30 EndZ=0
    g11: LineSegment StartX=-14.2 StartY=-30 StartZ=0 EndX=-14.2 EndY=-27.5 EndZ=0
    g12: LineSegment StartX=-14.2 StartY=-27.5 StartZ=0 EndX=-11.2 EndY=-27.5 EndZ=0
    g13: LineSegment StartX=-11.2 StartY=-27.5 StartZ=0 EndX=-11.2 EndY=-17 EndZ=0
    g14: LineSegment StartX=-11.2 StartY=-17 StartZ=0 EndX=-12.7 EndY=-17 EndZ=0
    g15: LineSegment StartX=-12.7 StartY=-17 StartZ=0 EndX=-12.7 EndY=-15 EndZ=0
    g16: LineSegment StartX=14.2 StartY=30 StartZ=0 EndX=10 EndY=30 EndZ=0
    g17: LineSegment StartX=10 StartY=30 StartZ=0 EndX=10 EndY=15 EndZ=0
    g18: LineSegment StartX=10 StartY=15 StartZ=0 EndX=12.7 EndY=15 EndZ=0
    g19: LineSegment StartX=12.7 StartY=15 StartZ=0 EndX=12.7 EndY=17 EndZ=0
    g20: LineSegment StartX=12.7 StartY=17 StartZ=0 EndX=11.2 EndY=17 EndZ=0
    g21: LineSegment StartX=11.2 StartY=17 StartZ=0 EndX=11.2 EndY=27.5 EndZ=0
    g22: LineSegment StartX=11.2 StartY=27.5 StartZ=0 EndX=14.2 EndY=27.5 EndZ=0
    g23: LineSegment StartX=14.2 StartY=27.5 StartZ=0 EndX=14.2 EndY=30 EndZ=0
    g24: LineSegment StartX=12.7 StartY=-15 StartZ=0 EndX=10 EndY=-15 EndZ=0
    g25: LineSegment StartX=10 StartY=-15 StartZ=0 EndX=10 EndY=-30 EndZ=0
    g26: LineSegment StartX=10 StartY=-30 StartZ=0 EndX=14.2 EndY=-30 EndZ=0
    g27: LineSegment StartX=14.2 StartY=-30 StartZ=0 EndX=14.2 EndY=-27.5 EndZ=0
    g28: LineSegment StartX=14.2 StartY=-27.5 StartZ=0 EndX=11.2 EndY=-27.5 EndZ=0
    g29: LineSegment StartX=11.2 StartY=-27.5 StartZ=0 EndX=11.2 EndY=-17 EndZ=0
    g30: LineSegment StartX=11.2 StartY=-17 StartZ=0 EndX=12.7 EndY=-17 EndZ=0
    g31: LineSegment StartX=12.7 StartY=-17 StartZ=0 EndX=12.7 EndY=-15 EndZ=0
  constraints (92):
    c: Vertical(g0)
    c: Coincident(g1,g0)
    c: Horizontal(g1)
    c: Coincident(g2,g1)
    c: Vertical(g2)
    c: Coincident(g3,g2)
    c: Horizontal(g3)
    c: Coincident(g4,g3)
    c: Vertical(g4)
    c: Coincident(g5,g4)
    c: Horizontal(g5)
    c: Coincident(g7,g6)
    c: Coincident(g7,g0)
    c: Horizontal(g7)
    c: Coincident(g6,g5)
    c: DistanceX(g7,g7) = 4.2
    c: DistanceX(g5,g5) = 3
    c: DistanceY(g2,g2) = 2
    c: DistanceY(g6,g6) = 2.5
    c: DistanceY(g4,g4) = 10.5
    c: Coincident(g0,g-6)
    c: Coincident(g8,g9)
    c: Vertical(g9)
    c: Coincident(g9,g10)
    c: Coincident(g10,g11)
    c: Coincident(g11,g12)
    c: Coincident(g12,g13)
    c: Vertical(g13)
    c: Coincident(g13,g14)
    c: Coincident(g14,g15)
    c: Coincident(g15,g8)
    c: Equal(g7,g10)
    c: Vertical(g11)
    c: Equal(g13,g4)
    c: Equal(g9,g0)
    c: Equal(g11,g6)
    c: Coincident(g8,g-4)
    c: Coincident(g16,g17)
    c: Vertical(g17)
    c: Coincident(g17,g18)
    c: Coincident(g18,g19)
    c: Vertical(g19)
    c: Coincident(g19,g20)
    c: Coincident(g20,g21)
    c: Vertical(g21)
    c: Coincident(g21,g22)
    c: Coincident(g22,g23)
    c: Coincident(g23,g16)
    c: Vertical(g23)
    c: Equal(g0,g17)
    c: Equal(g16,g7)
    c: Equal(g2,g19)
    c: Equal(g6,g23)
    c: Coincident(g-3,g16)
    c: Coincident(g24,g25)
    c: Vertical(g25)
    c: Coincident(g25,g26)
    c: Coincident(g26,g27)
    c: Vertical(g27)
    c: Coincident(g27,g28)
    c: Coincident(g28,g29)
    c: Vertical(g29)
    c: Coincident(g29,g30)
    c: Coincident(g30,g31)
    c: Coincident(g31,g24)
    c: Equal(g8,g24)
    c: Equal(g10,g26)
    c: Equal(g11,g27)
    c: Equal(g15,g31)
    c: Equal(g9,g25)
    c: Coincident(g24,g-5)
    c: Angle(g17,g16) = 1.5708
    c: Angle(g21,g22) = 1.5708
    c: Angle(g18,g17) = 1.5708
    c: Angle(g20,g21) = 1.5708
    c: Angle(g25,g24) = 1.5708
    c: Angle(g29,g30) = 1.5708
    c: Angle(g28,g29) = 1.5708
    c: Angle(g26,g25) = 1.5708
    c: Angle(g14,g13) = 1.5708
    c: Angle(g13,g12) = 1.5708
    c: Angle(g9,g10) = 1.5708
    c: Angle(g8,g9) = 1.5708
    c: DistanceX(g3,g3) = 1.5
    c: Angle(g6,g7) = 1.5708
    c: Equal(g20,g3)
    c: Equal(g3,g14)
    c: Angle(g15,g8) = 1.5708
    c: Equal(g12,g5)
    c: Equal(g28,g5)
    c: Equal(g5,g22)
    c: Angle(g24,g31) = 1.5708
FEATURE [PartDesign::Body] Body001  label="SideView"
  Group = -> [Sketch,Sketch012]
  Origin = -> Origin001
FEATURE [Sketcher::SketchObject] Sketch013  label="StatorCuttingAreasSketch"
  ExternalGeometry = -> [Sketch008,Sketch003]
  MapMode = 5
  Support = -> [XY_Plane]
  expr: Constraints[35] = Variables.connectionWidth + Variables.connectionThickness * 2
  expr: Constraints[34] = (Variables.connectionHeight + Variables.connectionThickness) * 2
  expr: Constraints[25] = Variables.connectionWidth
  expr: Constraints[24] = Variables.connectionHeight * 2
  expr: Constraints[9] = Variables.spokeBridgeHeight
  expr: Constraints[2] = Variables.tipHeight * (1 - Variables.tipHeightReduction / 100)
  sketch-geometry (30):
    g0: LineSegment [constr] StartX=15.2132 StartY=7.55502 StartZ=0 EndX=13.7097 EndY=7.00779 EndZ=0
    g1: LineSegment [constr] StartX=16.5102 StartY=3.99135 StartZ=0 EndX=15.0067 EndY=3.44412 EndZ=0
    g2: LineSegment StartX=13.7097 StartY=7.00779 StartZ=0 EndX=13.8976 EndY=7.07619 EndZ=0
    g3: LineSegment StartX=15.1947 StartY=3.51253 StartZ=0 EndX=15.0067 EndY=3.44412 EndZ=0
    g4: ArcOfCircle CenterX=0 CenterY=0 CenterZ=0 NormalX=0 NormalY=0 NormalZ=1 AngleXU=0 Radius=15.3969 StartAngle=0.225598 EndAngle=0.472533
    g5: ArcOfCircle CenterX=0 CenterY=0 CenterZ=0 NormalX=0 NormalY=0 NormalZ=1 AngleXU=0 Radius=15.5954 StartAngle=0.227178 EndAngle=0.470954
    g6: ArcOfEllipse CenterX=20.1593 CenterY=16.9157 CenterZ=0 NormalX=0 NormalY=0 NormalZ=1 MajorRadius=6 MinorRadius=2 AngleXU=-0.872665 StartAngle=-1.8e-15 EndAngle=1.5708
    g7: LineSegment [constr] StartX=24.016 StartY=12.3194 StartZ=0 EndX=16.3026 EndY=21.5119 EndZ=0
    g8: LineSegment [constr] StartX=21.6914 StartY=18.2012 StartZ=0 EndX=18.6272 EndY=15.6301 EndZ=0
    g9: GeomPoint X=23.7955 Y=12.5823 Z=0
    g10: GeomPoint X=16.5232 Y=21.2491 Z=0
    g11: ArcOfEllipse CenterX=20.1593 CenterY=16.9157 CenterZ=0 NormalX=0 NormalY=0 NormalZ=1 MajorRadius=6.3 MinorRadius=2.3 AngleXU=-0.872665 StartAngle=-9e-16 EndAngle=1.5708
    g12: LineSegment [constr] StartX=24.2089 StartY=12.0896 StartZ=0 EndX=16.1097 EndY=21.7417 EndZ=0
    g13: LineSegment [constr] StartX=21.9212 StartY=18.3941 StartZ=0 EndX=18.3974 EndY=15.4373 EndZ=0
    g14: GeomPoint X=23.9294 Y=12.4227 Z=0
    g15: GeomPoint X=16.3893 Y=21.4086 Z=0
    g16: LineSegment StartX=21.6914 StartY=18.2012 StartZ=0 EndX=21.9212 EndY=18.3941 EndZ=0
    g17: LineSegment StartX=24.016 StartY=12.3194 StartZ=0 EndX=24.2089 EndY=12.0896 EndZ=0
    g18: ArcOfEllipse CenterX=26.3161 CenterY=-1.6e-15 CenterZ=0 NormalX=0 NormalY=0 NormalZ=1 MajorRadius=6.3 MinorRadius=2.3 AngleXU=-1.5708 StartAngle=1.5708 EndAngle=3.14159
    g19: LineSegment [constr] StartX=26.3161 StartY=-6.3 StartZ=0 EndX=26.3161 EndY=6.3 EndZ=0
    g20: LineSegment [constr] StartX=28.6161 StartY=0 StartZ=0 EndX=24.0161 EndY=-3.2e-15 EndZ=0
    g21: GeomPoint X=26.3161 Y=-5.86515 Z=0
    g22: GeomPoint X=26.3161 Y=5.86515 Z=0
    g23: ArcOfEllipse CenterX=26.3161 CenterY=-1.4e-15 CenterZ=0 NormalX=0 NormalY=0 NormalZ=1 MajorRadius=6 MinorRadius=2 AngleXU=-1.5708 StartAngle=1.5708 EndAngle=3.14159
    g24: LineSegment [constr] StartX=26.3161 StartY=-6 StartZ=0 EndX=26.3161 EndY=6 EndZ=0
    g25: LineSegment [constr] StartX=28.3161 StartY=0 StartZ=0 EndX=24.3161 EndY=-2.7e-15 EndZ=0
    g26: GeomPoint X=26.3161 Y=-5.65685 Z=0
    g27: GeomPoint X=26.3161 Y=5.65685 Z=0
    g28: LineSegment StartX=26.3161 StartY=6 StartZ=0 EndX=26.3161 EndY=6.3 EndZ=0
    g29: LineSegment StartX=28.3161 StartY=-5e-16 StartZ=0 EndX=28.6161 EndY=0 EndZ=0
  constraints (54):
    c: Coincident(g0,g-3)
    c: PointOnObject(g0,g-3)
    c: Distance(g0) = 1.6
    c: Coincident(g1,g-4)
    c: Equal(g1,g0)
    c: Coincident(g2,g0)
    c: PointOnObject(g2,g0)
    c: PointOnObject(g3,g1)
    c: Coincident(g3,g1)
    c: Distance(g3) = 0.2
    c: Coincident(g4,g-1)
    c: Coincident(g4,g2)
    c: Coincident(g4,g3)
    c: Coincident(g5,g4)
    c: Coincident(g5,g3)
    c: Coincident(g5,g2)
    c: InternalAlignment(g7-g10 -> g6) x4
    c: PointOnObject(g6,g-5)
    c: PointOnObject(g6,g-8)
    c: Tangent(g-8,g8)
    c: PointOnObject(g7,g-5)
    c: Distance(g8) = 4
    c: Distance(g7) = 12
    c: InternalAlignment(g12-g15 -> g11) x4
    c: Parallel(g12,g7)
    c: PointOnObject(g11,g-5)
    c: PointOnObject(g11,g-8)
    c: Coincident(g11,g6)
    c: Distance(g13) = 4.6
    c: Distance(g12) = 12.6
    c: Coincident(g16,g6)
    c: Coincident(g16,g11)
    c: Coincident(g17,g11)
    c: Coincident(g17,g6)
    c: InternalAlignment(g19-g22 -> g18) x4
    c: PointOnObject(g18,g-6)
    c: PointOnObject(g18,g-7)
    c: Parallel(g19,g-6)
    c: PointOnObject(g20,g-7)
    c: PointOnObject(g-6,g19)
    c: Equal(g19,g12)
    c: Equal(g20,g13)
    c: InternalAlignment(g24-g27 -> g23) x4
    c: Parallel(g24,g-6)
    c: PointOnObject(g24,g-6)
    c: PointOnObject(g25,g-7)
    c: PointOnObject(g23,g-7)
    c: PointOnObject(g23,g-6)
    c: Equal(g24,g7)
    c: Equal(g25,g8)
    c: Coincident(g28,g23)
    c: Coincident(g28,g18)
    c: Coincident(g29,g23)
    c: Coincident(g29,g18)
FEATURE [PartDesign::Body] Body  label="TopView"
  Group = -> [Sketch003,Sketch005,Sketch006,Sketch007,Sketch008,Sketch010,Sketch011,Sketch013]
  Origin = -> Origin
FEATURE [Surface::Filling] Surface005  label="SpokeClosingBridge_Surface"
  Anisotropy = false
  BoundaryEdges = -> [Sketch013]
  BoundaryOrder = [0,0,0,0]
  Degree = 3
  Iterations = 2
  MaximumDegree = 8
  MaximumSegments = 9
  PointsOnCurve = 15
  TolAngular = 0.01
  TolCurvature = 0.1
  Tolerance2d = 1e-05
  Tolerance3d = 0.0001
FEATURE [Surface::Filling] Surface006  label="SpokeRightConnection_Surface"
  Anisotropy = false
  BoundaryEdges = -> [Sketch013]
  BoundaryOrder = [0,0,0,0]
  Degree = 3
  Iterations = 2
  MaximumDegree = 8
  MaximumSegments = 9
  PointsOnCurve = 15
  TolAngular = 0.01
  TolCurvature = 0.1
  Tolerance2d = 1e-05
  Tolerance3d = 0.0001
FEATURE [Surface::Filling] Surface007  label="SpokeLeftConnection_Surface"
  Anisotropy = false
  BoundaryEdges = -> [Sketch013]
  BoundaryOrder = [0,0,0,0]
  Degree = 3
  Iterations = 2
  MaximumDegree = 8
  MaximumSegments = 9
  PointsOnCurve = 15
  TolAngular = 0.01
  TolCurvature = 0.1
  Tolerance2d = 1e-05
  Tolerance3d = 0.0001
